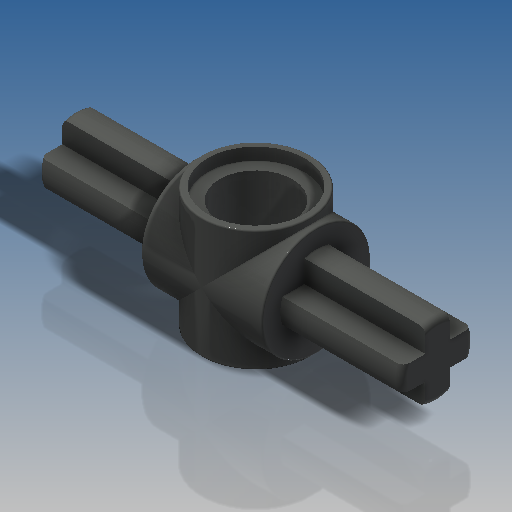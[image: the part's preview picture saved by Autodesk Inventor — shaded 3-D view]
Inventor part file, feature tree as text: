
AUTODESK INVENTOR PART (.ipt)
format: ipt  version: 2019.4 (Build 234330000, 330)  size: 304,640 bytes
history: native  units: in
note: dims shown in document units (in); Inventor stores cm internally (conversion verified against a paired STEP export)
features: extrude x4, sketch x2, revolve x1, pattern_circular x1, fillet x1
ambient origin geometry x8: Origin, YZ Plane, XZ Plane, XY Plane, X Axis, Y Axis, Z Axis, Center Point
bodies: Solid1 (feature_tree)
feature tree (9):
  sketch  "Sketch2"  dims[d0=0.189in d1=0.252in]
  extrude  "Extrusion1"  Depth=0.252in
  revolve  "Revolution1"  [1 undecoded]
  extrude  "Extrusion4"  Depth=0.0157in
  pattern_circular  "Circular Pattern1"  [2 undecoded]
  extrude  "Extrusion2"  TaperAngle=0.0deg  [1 undecoded]
  extrude  "Extrusion3"  TaperAngle=90.0deg  [1 undecoded]
  fillet  "Fillet1"  Radius=0.315in
  sketch  "Sketch3"  dims[d2=0.2835in d3=0.1575in d4=0.2835in d5=0.315in d6=0.0in d7=90.0deg d8=0.315in d9=0.0in d10=0.252in d11=0.0in d12=0.063in d13=0.189in d14=0.315in d15=0.0in d16=0.0039in d17=0.0157in d18=0.0in d19=0.0in d20=0.7874in d21=360.0deg]
note: 5 required parameter values undecoded (feature->parameter linkage not recoverable at this tier; creation-order binding heuristic only, values carry confidence <= 0.55)